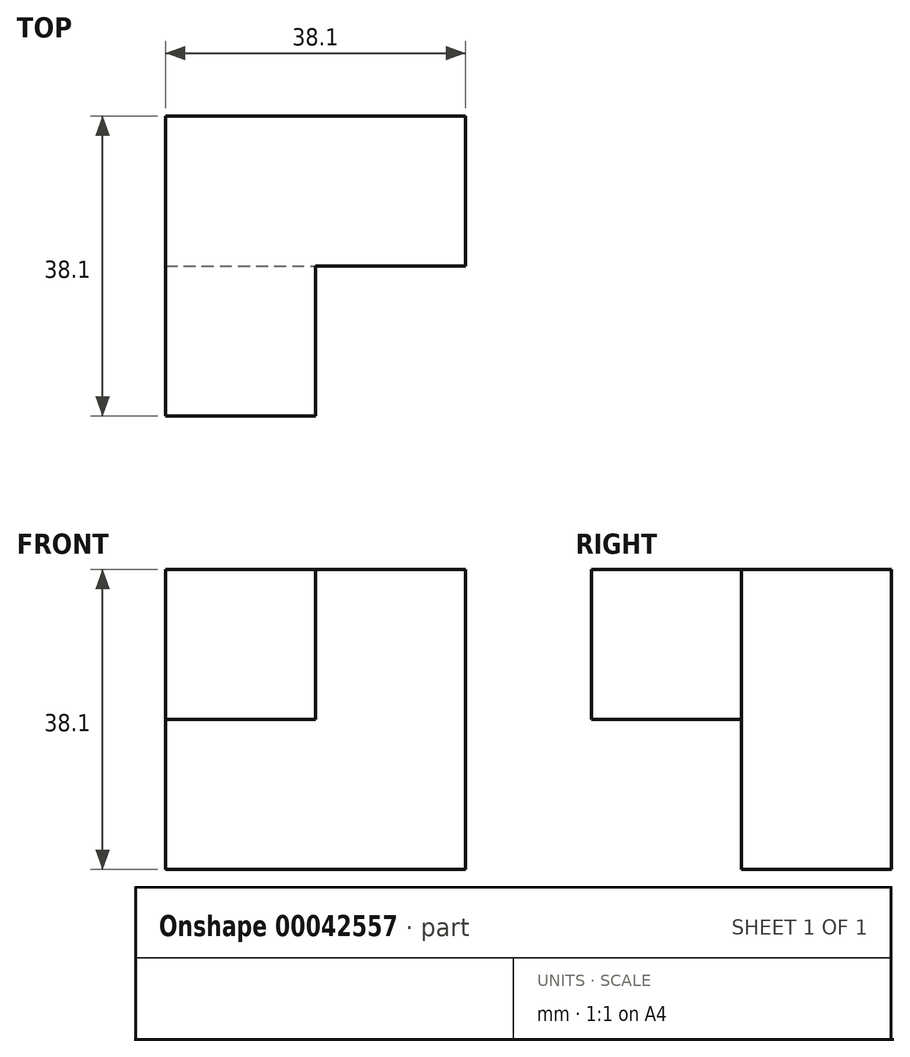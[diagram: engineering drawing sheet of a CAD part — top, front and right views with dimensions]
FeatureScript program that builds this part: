
annotation { "Feature Type Name" : "Feature", "Feature Type Description" : "" }
export const myFeature = defineFeature(function(context is Context, id is Id, definition is map)
    precondition{}
    {
        {
            var Q0;
            Q0=qCreatedBy(makeId("Right.planeOp"),FACE);
            var sketch = newSketch(context, id + "F0", { "sketchPlane" : qUnion([Q0])});
            skLineSegment(sketch, "E0.bottom", {"start": v(0, 0) * mm, "end": v(-19.05, 0) * mm});
            skLineSegment(sketch, "E0.top", {"start": v(0, 38.1) * mm, "end": v(-19.05, 38.1) * mm});
            skLineSegment(sketch, "E0.left", {"start": v(0, 0) * mm, "end": v(0, 38.1) * mm});
            skLineSegment(sketch, "E0.right", {"start": v(-19.05, 0) * mm, "end": v(-19.05, 38.1) * mm});
            skLineSegment(sketch, "E1.bottom", {"start": v(-19.05, 38.1) * mm, "end": v(-38.1, 38.1) * mm});
            skLineSegment(sketch, "E1.top", {"start": v(-19.05, 19.05) * mm, "end": v(-38.1, 19.05) * mm});
            skLineSegment(sketch, "E1.left", {"start": v(-19.05, 38.1) * mm, "end": v(-19.05, 19.05) * mm});
            skLineSegment(sketch, "E1.right", {"start": v(-38.1, 38.1) * mm, "end": v(-38.1, 19.05) * mm});
            skSolve(sketch);
        }
        {
            var Q0;
            Q0=qSketchRegion(id+"F0",true);
            extrude(context, id + "F1", {"entities" : qUnion([Q0]), "oppositeDirection" : true, "depth" : 19.05 * mm});
        }
        {
            var Q0;
            Q0=qCreatedBy(makeId("Right.planeOp"),FACE);
            var sketch = newSketch(context, id + "F2", { "sketchPlane" : qUnion([Q0])});
            skLineSegment(sketch, "E2.bottom", {"start": v(0, 38.1) * mm, "end": v(-38.1, 38.1) * mm});
            skLineSegment(sketch, "E2.top", {"start": v(0, 19.05) * mm, "end": v(-38.1, 19.05) * mm});
            skLineSegment(sketch, "E2.left", {"start": v(0, 38.1) * mm, "end": v(0, 19.05) * mm});
            skLineSegment(sketch, "E2.right", {"start": v(-38.1, 38.1) * mm, "end": v(-38.1, 19.05) * mm});
            skSolve(sketch);
        }
        {
            var Q0;
            Q0=qSketchRegion(id+"F2",true);
            extrude(context, id + "F3", {"entities" : qUnion([Q0]), "operationType" : NewBodyOperationType.ADD, "oppositeDirection" : true, "depth" : 38.1 * mm});
        }
        {
            var Q0;
            Q0=makeQuery(id+"F1.opExtrude","CAP_FACE",FACE,{"disambiguationData":[OSD([sQuery(id+"F0.wireOp",EDGE,"E0.bottom"),sQuery(id+"F0.wireOp",EDGE,"E0.top"),sQuery(id+"F0.wireOp",EDGE,"E0.left"),sQuery(id+"F0.wireOp",EDGE,"E0.right"),sQuery(id+"F0.wireOp",EDGE,"E1.bottom"),sQuery(id+"F0.wireOp",EDGE,"E1.top"),sQuery(id+"F0.wireOp",EDGE,"E1.right")])],"isStart":false});
            extrude(context, id + "F4", {"entities" : qUnion([Q0]), "operationType" : NewBodyOperationType.ADD, "depth" : 19.05 * mm});
        }
        {
            var Q0;
            Q0=makeQuery(id+"F3.boolean.opBoolean","MERGE",FACE,{"derivedFrom":[makeQuery(id+"F1.opExtrude","SWEPT_FACE",FACE,{"disambiguationData":[OSD([sQuery(id+"F0.wireOp",EDGE,"E0.top"),sQuery(id+"F0.wireOp",EDGE,"E1.bottom")])]}),makeQuery(id+"F3.opExtrude","SWEPT_FACE",FACE,{"disambiguationData":[OSD([sQuery(id+"F2.wireOp",EDGE,"E2.bottom")])]})]});
            var sketch = newSketch(context, id + "F5", { "sketchPlane" : qUnion([Q0])});
            skLineSegment(sketch, "E3.bottom", {"start": v(0, -38.1) * mm, "end": v(-19.05, -38.1) * mm});
            skLineSegment(sketch, "E3.top", {"start": v(0, -19.05) * mm, "end": v(-19.05, -19.05) * mm});
            skLineSegment(sketch, "E3.left", {"start": v(0, -38.1) * mm, "end": v(0, -19.05) * mm});
            skLineSegment(sketch, "E3.right", {"start": v(-19.05, -38.1) * mm, "end": v(-19.05, -19.05) * mm});
            skSolve(sketch);
        }
        {
            var Q0;
            Q0=makeQuery(id+"F5.imprint","IMPRINT",FACE,{"disambiguationData":[TD([[makeQuery(id+"F5.imprint","IMPRINT",EDGE,{"derivedFrom":sQuery(id+"F5.wireOp",EDGE,"E3.bottom")}),1.0]])]});
            extrude(context, id + "F6", {"entities" : qUnion([Q0]), "operationType" : NewBodyOperationType.REMOVE, "oppositeDirection" : true, "depth" : 25.4 * mm});
        }
    });
